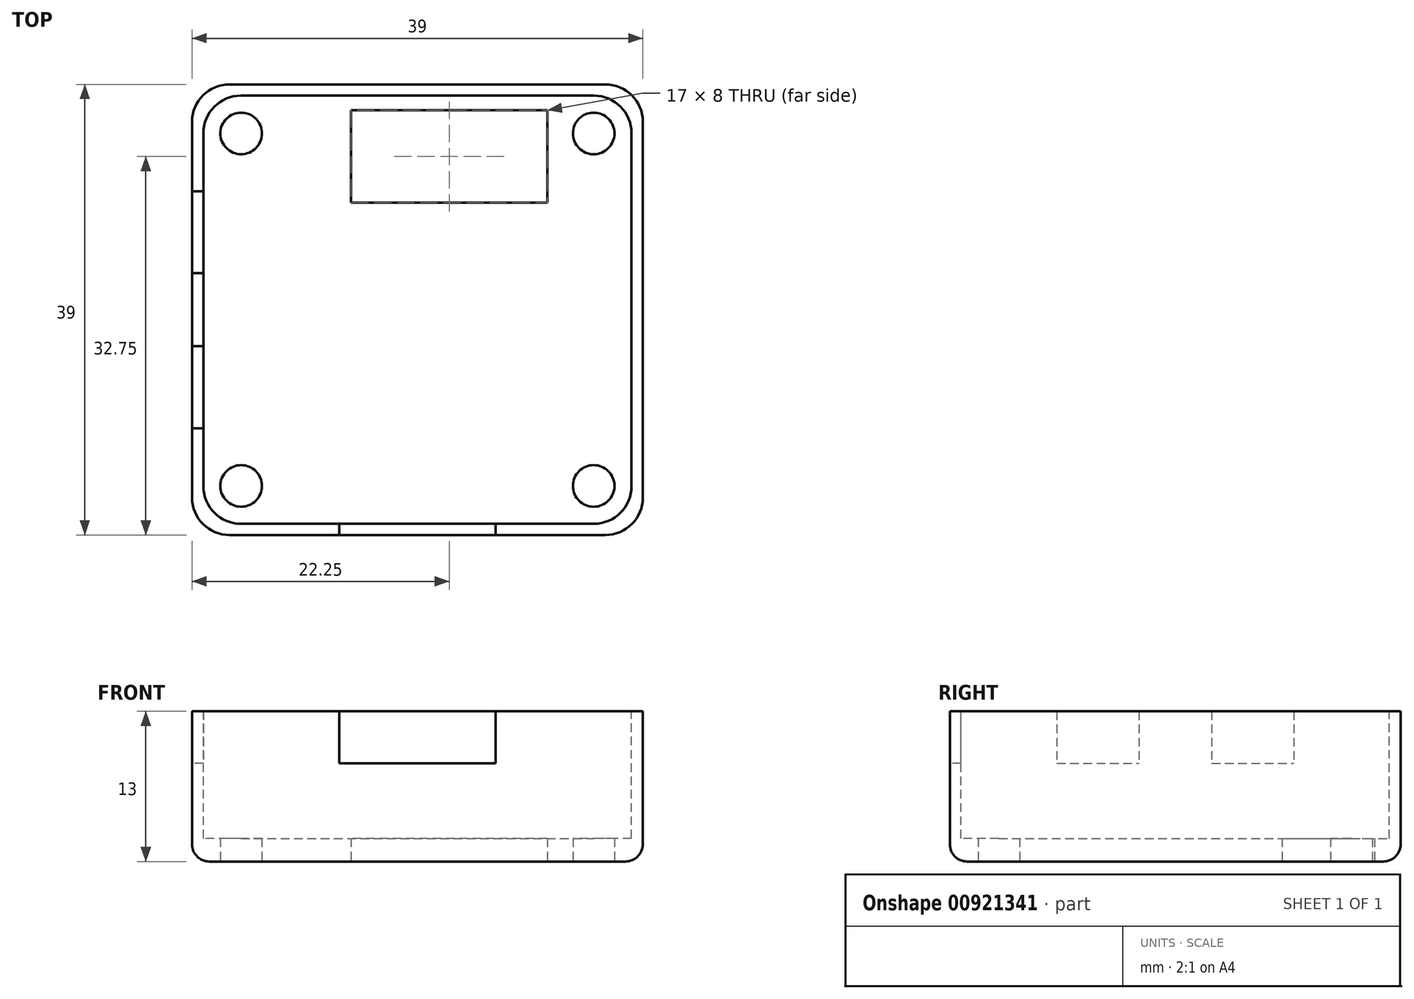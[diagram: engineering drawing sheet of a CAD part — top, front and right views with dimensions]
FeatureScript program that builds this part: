
annotation { "Feature Type Name" : "Feature", "Feature Type Description" : "" }
export const myFeature = defineFeature(function(context is Context, id is Id, definition is map)
    precondition{}
    {
        {
            var Q0;
            Q0=qCreatedBy(makeId("Top.planeOp"),FACE);
            var sketch = newSketch(context, id + "F0", { "sketchPlane" : qUnion([Q0])});
            skLineSegment(sketch, "E0.bottom", {"start": v(19.5, 19.5) * mm, "end": v(-19.5, 19.5) * mm});
            skLineSegment(sketch, "E0.top", {"start": v(19.5, -19.5) * mm, "end": v(-19.5, -19.5) * mm});
            skLineSegment(sketch, "E0.left", {"start": v(19.5, 19.5) * mm, "end": v(19.5, -19.5) * mm});
            skLineSegment(sketch, "E0.right", {"start": v(-19.5, 19.5) * mm, "end": v(-19.5, -19.5) * mm});
            skPoint(sketch, "E0.middle", {"position": v(0, 0) * mm});
            skSolve(sketch);
        }
        {
            var Q0;
            Q0 = qSketchRegion(id + "F0", true);
            extrude(context, id + "F1", {"entities" : qUnion([Q0]), "oppositeDirection" : true, "depth" : 13 * mm, "offsetDistance" : 25 * mm});
        }
        {
            var Q0;
            Q0=makeQuery(id+"F1.opExtrude","CAP_FACE",FACE,{"disambiguationData":[OSD([sQuery(id+"F0.wireOp",EDGE,"E0.bottom"),sQuery(id+"F0.wireOp",EDGE,"E0.top"),sQuery(id+"F0.wireOp",EDGE,"E0.left"),sQuery(id+"F0.wireOp",EDGE,"E0.right")])],"isStart":false});
            var sketch = newSketch(context, id + "F2", { "sketchPlane" : qUnion([Q0])});
            skLineSegment(sketch, "E1.bottom", {"start": v(15.25, 18.5) * mm, "end": v(-15.25, 18.5) * mm, "construction": true});
            skLineSegment(sketch, "E1.top", {"start": v(15.25, -18.5) * mm, "end": v(-15.25, -18.5) * mm, "construction": true});
            skLineSegment(sketch, "E1.left", {"start": v(18.5, 15.25) * mm, "end": v(18.5, -15.25) * mm, "construction": true});
            skLineSegment(sketch, "E1.right", {"start": v(-18.5, 15.25) * mm, "end": v(-18.5, -15.25) * mm, "construction": true});
            skPoint(sketch, "E1.middle", {"position": v(0, 0) * mm});
            skPoint(sketch, "E2.visualSharp", {"position": v(-18.5, 18.5) * mm});
            skArc(sketch, "E2.filletArc", {"start": v(-15.25, 18.5) * mm, "mid": v(-17.55, 17.55) * mm, "end": v(-18.5, 15.25) * mm, "construction": true});
            skPoint(sketch, "E3.visualSharp", {"position": v(18.5, 18.5) * mm});
            skArc(sketch, "E3.filletArc", {"start": v(18.5, 15.25) * mm, "mid": v(17.55, 17.55) * mm, "end": v(15.25, 18.5) * mm, "construction": true});
            skPoint(sketch, "E4.visualSharp", {"position": v(18.5, -18.5) * mm});
            skArc(sketch, "E4.filletArc", {"start": v(15.25, -18.5) * mm, "mid": v(17.55, -17.55) * mm, "end": v(18.5, -15.25) * mm, "construction": true});
            skPoint(sketch, "E5.visualSharp", {"position": v(-18.5, -18.5) * mm});
            skArc(sketch, "E5.filletArc", {"start": v(-18.5, -15.25) * mm, "mid": v(-17.55, -17.55) * mm, "end": v(-15.25, -18.5) * mm, "construction": true});
            skCircle(sketch, "E6", {"center": v(-15.25, 15.25) * mm, "radius": 1.8 * mm});
            skCircle(sketch, "E7", {"center": v(15.25, 15.25) * mm, "radius": 1.8 * mm});
            skCircle(sketch, "E8", {"center": v(-15.25, -15.25) * mm, "radius": 1.8 * mm});
            skCircle(sketch, "E9", {"center": v(15.25, -15.25) * mm, "radius": 1.8 * mm});
            skLineSegment(sketch, "E10.bottom", {"start": v(-5.75, -17.25) * mm, "end": v(11.25, -17.25) * mm});
            skLineSegment(sketch, "E10.top", {"start": v(-5.75, -9.25) * mm, "end": v(11.25, -9.25) * mm});
            skLineSegment(sketch, "E10.left", {"start": v(-5.75, -17.25) * mm, "end": v(-5.75, -9.25) * mm});
            skLineSegment(sketch, "E10.right", {"start": v(11.25, -17.25) * mm, "end": v(11.25, -9.25) * mm});
            skSolve(sketch);
        }
        {
            var Q0;
            Q0=makeQuery(id+"F1.opExtrude","SWEPT_EDGE",EDGE,{"disambiguationData":[OSD([sQuery(id+"F0.wireOp",EDGE,"E0.top"),sQuery(id+"F0.wireOp",EDGE,"E0.right")])]});
            var Q1;
            Q1=makeQuery(id+"F1.opExtrude","SWEPT_EDGE",EDGE,{"disambiguationData":[OSD([sQuery(id+"F0.wireOp",EDGE,"E0.top"),sQuery(id+"F0.wireOp",EDGE,"E0.left")])]});
            var Q2;
            Q2=makeQuery(id+"F1.opExtrude","SWEPT_EDGE",EDGE,{"disambiguationData":[OSD([sQuery(id+"F0.wireOp",EDGE,"E0.bottom"),sQuery(id+"F0.wireOp",EDGE,"E0.left")])]});
            var Q3;
            Q3=makeQuery(id+"F1.opExtrude","SWEPT_EDGE",EDGE,{"disambiguationData":[OSD([sQuery(id+"F0.wireOp",EDGE,"E0.bottom"),sQuery(id+"F0.wireOp",EDGE,"E0.right")])]});
            fillet(context, id + "F3", {"entities" : qUnion([Q0, Q1, Q2, Q3]), "radius" : 3.25 * mm, "tangentPropagation" : true, "allowEdgeOverflow" : false});
        }
        {
            var Q0;
            Q0=qCreatedBy(makeId("Top.planeOp"),FACE);
            var sketch = newSketch(context, id + "F4", { "sketchPlane" : qUnion([Q0])});
            skLineSegment(sketch, "E11.bottom", {"start": v(-15.27, -18.52) * mm, "end": v(15.27, -18.52) * mm});
            skLineSegment(sketch, "E11.top", {"start": v(-15.27, 18.52) * mm, "end": v(15.27, 18.52) * mm});
            skLineSegment(sketch, "E11.left", {"start": v(-18.52, -15.27) * mm, "end": v(-18.52, 15.27) * mm});
            skLineSegment(sketch, "E11.right", {"start": v(18.52, -15.27) * mm, "end": v(18.52, 15.27) * mm});
            skPoint(sketch, "E11.middle", {"position": v(0, 0) * mm});
            skPoint(sketch, "E12.visualSharp", {"position": v(-18.52, 18.52) * mm});
            skArc(sketch, "E12.filletArc", {"start": v(-15.27, 18.52) * mm, "mid": v(-17.57, 17.57) * mm, "end": v(-18.52, 15.27) * mm});
            skPoint(sketch, "E13.visualSharp", {"position": v(18.52, 18.52) * mm});
            skArc(sketch, "E13.filletArc", {"start": v(18.52, 15.27) * mm, "mid": v(17.57, 17.57) * mm, "end": v(15.27, 18.52) * mm});
            skPoint(sketch, "E14.visualSharp", {"position": v(18.52, -18.52) * mm});
            skArc(sketch, "E14.filletArc", {"start": v(15.27, -18.52) * mm, "mid": v(17.57, -17.57) * mm, "end": v(18.52, -15.27) * mm});
            skPoint(sketch, "E15.visualSharp", {"position": v(-18.52, -18.52) * mm});
            skArc(sketch, "E15.filletArc", {"start": v(-18.52, -15.27) * mm, "mid": v(-17.57, -17.57) * mm, "end": v(-15.27, -18.52) * mm});
            skSolve(sketch);
        }
        {
            var Q0;
            Q0 = qSketchRegion(id + "F4", true);
            extrude(context, id + "F5", {"entities" : qUnion([Q0]), "operationType" : NewBodyOperationType.REMOVE, "oppositeDirection" : true, "depth" : 11 * mm, "offsetDistance" : 25 * mm});
        }
        {
            var Q0;
            Q0 = qSketchRegion(id + "F2", true);
            extrude(context, id + "F6", {"entities" : qUnion([Q0]), "operationType" : NewBodyOperationType.REMOVE, "endBound" : BoundingType.THROUGH_ALL, "oppositeDirection" : true, "depth" : 25 * mm, "offsetDistance" : 25 * mm});
        }
        {
            var Q0;
            Q0=makeQuery(id+"F1.opExtrude","CAP_EDGE",EDGE,{"disambiguationData":[OSD([sQuery(id+"F0.wireOp",EDGE,"E0.top")])],"isStart":false});
            fillet(context, id + "F7", {"entities" : qUnion([Q0]), "radius" : 1.5 * mm, "tangentPropagation" : true, "allowEdgeOverflow" : false});
        }
        {
            var Q0;
            Q0=qCreatedBy(makeId("Right.planeOp"),FACE);
            cPlane(context, id + "F8", {"entities" : qUnion([Q0]), "cplaneType" : CPlaneType.OFFSET, "offset" : 15.25 * mm, "width" : 150 * mm, "height" : 150 * mm});
        }
        {
            var Q0;
            Q0=qCreatedBy(makeId("Right.planeOp"),FACE);
            cPlane(context, id + "F9", {"entities" : qUnion([Q0]), "cplaneType" : CPlaneType.OFFSET, "offset" : 15.25 * mm, "oppositeDirection" : true, "width" : 150 * mm, "height" : 150 * mm});
        }
        {
            var Q0;
            Q0=qCreatedBy(makeId("Front.planeOp"),FACE);
            cPlane(context, id + "F10", {"entities" : qUnion([Q0]), "cplaneType" : CPlaneType.OFFSET, "offset" : 15.25 * mm, "width" : 150 * mm, "height" : 150 * mm});
        }
        {
            var Q0;
            Q0=qCreatedBy(makeId("Front.planeOp"),FACE);
            cPlane(context, id + "F11", {"entities" : qUnion([Q0]), "cplaneType" : CPlaneType.OFFSET, "offset" : 15.25 * mm, "oppositeDirection" : true, "width" : 150 * mm, "height" : 150 * mm});
        }
        {
            var Q0;
            Q0=makeQuery(id+"F1.opExtrude","SWEPT_FACE",FACE,{"disambiguationData":[OSD([sQuery(id+"F0.wireOp",EDGE,"E0.right")])]});
            var sketch = newSketch(context, id + "F12", { "sketchPlane" : qUnion([Q0])});
            skLineSegment(sketch, "E16.bottom", {"start": v(10.25, 0) * mm, "end": v(3.15, 0) * mm});
            skLineSegment(sketch, "E16.top", {"start": v(10.25, -4.5) * mm, "end": v(3.15, -4.5) * mm});
            skLineSegment(sketch, "E16.left", {"start": v(10.25, 0) * mm, "end": v(10.25, -4.5) * mm});
            skLineSegment(sketch, "E16.right", {"start": v(3.15, 0) * mm, "end": v(3.15, -4.5) * mm});
            skLineSegment(sketch, "E17.bottom", {"start": v(-3.15, 0) * mm, "end": v(-10.25, 0) * mm});
            skLineSegment(sketch, "E17.top", {"start": v(-3.15, -4.5) * mm, "end": v(-10.25, -4.5) * mm});
            skLineSegment(sketch, "E17.left", {"start": v(-3.15, 0) * mm, "end": v(-3.15, -4.5) * mm});
            skLineSegment(sketch, "E17.right", {"start": v(-10.25, 0) * mm, "end": v(-10.25, -4.5) * mm});
            skSolve(sketch);
        }
        {
            var Q0;
            Q0 = qSketchRegion(id + "F12", true);
            extrude(context, id + "F13", {"entities" : qUnion([Q0]), "operationType" : NewBodyOperationType.REMOVE, "endBound" : BoundingType.UP_TO_NEXT, "oppositeDirection" : true, "depth" : 25 * mm, "offsetDistance" : 25 * mm});
        }
        {
            var Q0;
            Q0=makeQuery(id+"F1.opExtrude","SWEPT_FACE",FACE,{"disambiguationData":[OSD([sQuery(id+"F0.wireOp",EDGE,"E0.top")])]});
            var sketch = newSketch(context, id + "F14", { "sketchPlane" : qUnion([Q0])});
            skLineSegment(sketch, "E18.bottom", {"start": v(6.75, 0) * mm, "end": v(-6.75, 0) * mm});
            skLineSegment(sketch, "E18.top", {"start": v(6.75, -4.5) * mm, "end": v(-6.75, -4.5) * mm});
            skLineSegment(sketch, "E18.left", {"start": v(6.75, 0) * mm, "end": v(6.75, -4.5) * mm});
            skLineSegment(sketch, "E18.right", {"start": v(-6.75, 0) * mm, "end": v(-6.75, -4.5) * mm});
            skSolve(sketch);
        }
        {
            var Q0;
            Q0 = qSketchRegion(id + "F14", true);
            extrude(context, id + "F15", {"entities" : qUnion([Q0]), "operationType" : NewBodyOperationType.REMOVE, "endBound" : BoundingType.UP_TO_NEXT, "oppositeDirection" : true, "depth" : 25 * mm, "offsetDistance" : 25 * mm});
        }
    });
